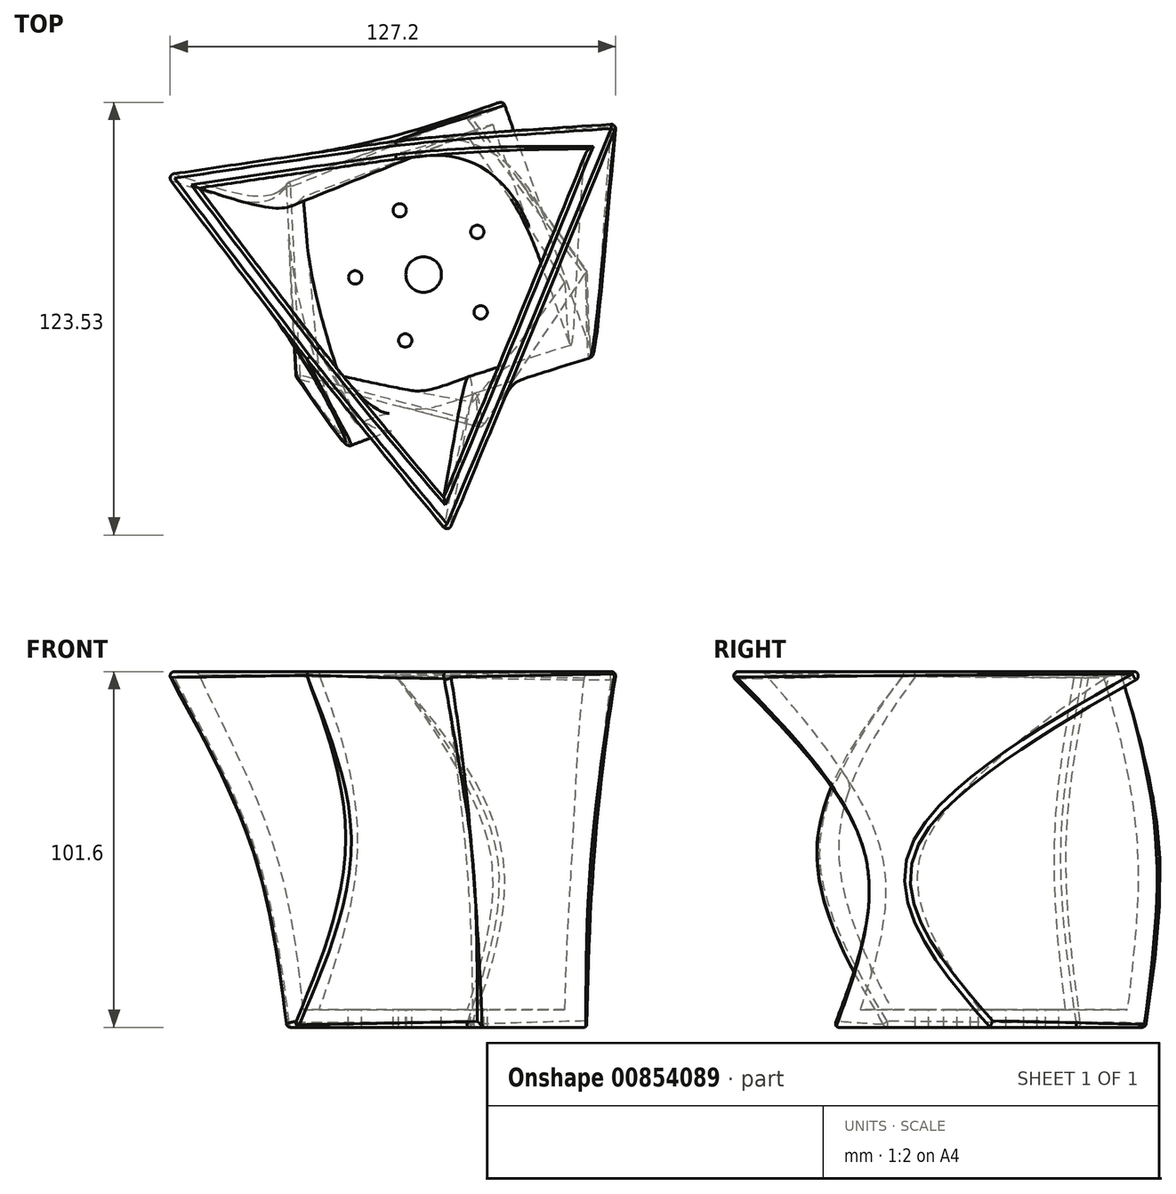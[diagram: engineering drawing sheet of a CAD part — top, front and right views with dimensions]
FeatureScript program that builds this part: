
annotation { "Feature Type Name" : "Feature", "Feature Type Description" : "" }
export const myFeature = defineFeature(function(context is Context, id is Id, definition is map)
    precondition{}
    {
        {
            var Q0;
            Q0=qCreatedBy(makeId("Top.planeOp"),FACE);
            var sketch = newSketch(context, id + "F0", { "sketchPlane" : qUnion([Q0])});
            skCircle(sketch, "E0.cCircle", {"center": v(0, 0) * mm, "radius": 38.1 * mm, "construction": true});
            skLineSegment(sketch, "E0.0", {"start": v(-39.1, 26.24) * mm, "end": v(12.87, 45.3) * mm});
            skLineSegment(sketch, "E0.1", {"start": v(12.87, 45.3) * mm, "end": v(47.06, 1.76) * mm});
            skLineSegment(sketch, "E0.2", {"start": v(47.06, 1.76) * mm, "end": v(16.21, -44.22) * mm});
            skLineSegment(sketch, "E0.3", {"start": v(16.21, -44.22) * mm, "end": v(-37.04, -29.08) * mm});
            skLineSegment(sketch, "E0.4", {"start": v(-37.04, -29.08) * mm, "end": v(-39.1, 26.24) * mm});
            skPoint(sketch, "E0.0.midPoint", {"position": v(-13.12, 35.77) * mm});
            skSolve(sketch);
        }
        {
            var Q0;
            Q0=qCreatedBy(makeId("Top.planeOp"),FACE);
            cPlane(context, id + "F1", {"entities" : qUnion([Q0]), "cplaneType" : CPlaneType.OFFSET, "offset" : 50.8 * mm, "width" : 152.4 * mm, "height" : 152.4 * mm});
        }
        {
            var Q0;
            Q0=qCreatedBy(id+"F1.planeOp",FACE);
            var sketch = newSketch(context, id + "F2", { "sketchPlane" : qUnion([Q0])});
            skCircle(sketch, "E1.cCircle", {"center": v(0, 0) * mm, "radius": 38.1 * mm, "construction": true});
            skLineSegment(sketch, "E1.0", {"start": v(-49.26, 21.84) * mm, "end": v(21.84, 49.26) * mm});
            skLineSegment(sketch, "E1.1", {"start": v(21.84, 49.26) * mm, "end": v(49.26, -21.84) * mm});
            skLineSegment(sketch, "E1.2", {"start": v(49.26, -21.84) * mm, "end": v(-21.84, -49.26) * mm});
            skLineSegment(sketch, "E1.3", {"start": v(-21.84, -49.26) * mm, "end": v(-49.26, 21.84) * mm});
            skPoint(sketch, "E1.0.midPoint", {"position": v(-13.71, 35.55) * mm});
            skSolve(sketch);
        }
        {
            var Q0;
            Q0=qCreatedBy(id+"F1.planeOp",FACE);
            cPlane(context, id + "F3", {"entities" : qUnion([Q0]), "cplaneType" : CPlaneType.OFFSET, "offset" : 50.8 * mm, "width" : 152.4 * mm, "height" : 152.4 * mm});
        }
        {
            var Q0;
            Q0=qCreatedBy(id+"F3.planeOp",FACE);
            var sketch = newSketch(context, id + "F4", { "sketchPlane" : qUnion([Q0])});
            skCircle(sketch, "E2.cCircle", {"center": v(-3.69, 0) * mm, "radius": 38.1 * mm, "construction": true});
            skLineSegment(sketch, "E2.0", {"start": v(-74.27, 28.73) * mm, "end": v(56.48, 46.76) * mm});
            skLineSegment(sketch, "E2.1", {"start": v(56.48, 46.76) * mm, "end": v(6.72, -75.49) * mm});
            skLineSegment(sketch, "E2.2", {"start": v(6.72, -75.49) * mm, "end": v(-74.27, 28.73) * mm});
            skPoint(sketch, "E2.0.midPoint", {"position": v(-8.9, 37.74) * mm});
            skSolve(sketch);
        }
        {
            var Q0;
            Q0=makeQuery(id+"F0.imprint","IMPRINT",FACE,{"disambiguationData":[TD([[makeQuery(id+"F0.imprint","IMPRINT",EDGE,{"derivedFrom":sQuery(id+"F0.wireOp",EDGE,"E0.0")}),-1.0]])]});
            var Q1;
            Q1=makeQuery(id+"F2.imprint","IMPRINT",FACE,{"disambiguationData":[TD([[makeQuery(id+"F2.imprint","IMPRINT",EDGE,{"derivedFrom":sQuery(id+"F2.wireOp",EDGE,"E1.0")}),-1.0]])]});
            var Q2;
            Q2=makeQuery(id+"F4.imprint","IMPRINT",FACE,{"disambiguationData":[TD([[makeQuery(id+"F4.imprint","IMPRINT",EDGE,{"derivedFrom":sQuery(id+"F4.wireOp",EDGE,"E2.0")}),-1.0]])]});
            loft(context, id + "F5", {"sheetProfilesArray" : [{ "sheetProfileEntities" : qUnion([Q0]) }, { "sheetProfileEntities" : qUnion([Q1]) }, { "sheetProfileEntities" : qUnion([Q2]) }]});
        }
        {
            var Q0;
            Q0=makeQuery(id+"F5.opLoft","CAP_FACE",FACE,{"disambiguationData":[OSD([makeQuery(id+"F4.imprint","IMPRINT",FACE,{"disambiguationData":[TD([[makeQuery(id+"F4.imprint","IMPRINT",EDGE,{"derivedFrom":sQuery(id+"F4.wireOp",EDGE,"E2.0")}),-1.0]])]})])],"isStart":true});
            shell(context, id + "F6", {"entities" : qUnion([Q0]), "thickness" : 5.08 * mm});
        }
        {
            var Q0;
            Q0=makeQuery(id+"F5.opLoft","CAP_FACE",FACE,{"disambiguationData":[OSD([makeQuery(id+"F4.imprint","IMPRINT",FACE,{"disambiguationData":[TD([[makeQuery(id+"F4.imprint","IMPRINT",EDGE,{"derivedFrom":sQuery(id+"F4.wireOp",EDGE,"E2.0")}),-1.0]])]})])],"isStart":true});
            var Q1;
            Q1=makeQuery(id+"F5.opLoft","SWEPT_FACE",FACE,{"disambiguationData":[OSD([sQuery(id+"F0.wireOp",EDGE,"E0.0"),sQuery(id+"F0.wireOp",EDGE,"E0.1"),sQuery(id+"F0.wireOp",EDGE,"E0.2"),sQuery(id+"F2.wireOp",EDGE,"E1.0"),sQuery(id+"F2.wireOp",EDGE,"E1.1"),sQuery(id+"F2.wireOp",EDGE,"E1.2"),sQuery(id+"F4.wireOp",EDGE,"E2.0"),sQuery(id+"F4.wireOp",EDGE,"E2.1"),sQuery(id+"F4.wireOp",EDGE,"E2.2")])]});
            var Q2;
            Q2=makeQuery(id+"F5.opLoft","SWEPT_FACE",FACE,{"disambiguationData":[OSD([sQuery(id+"F0.wireOp",EDGE,"E0.1"),sQuery(id+"F0.wireOp",EDGE,"E0.2"),sQuery(id+"F0.wireOp",EDGE,"E0.3"),sQuery(id+"F0.wireOp",EDGE,"E0.4"),sQuery(id+"F2.wireOp",EDGE,"E1.1"),sQuery(id+"F2.wireOp",EDGE,"E1.2"),sQuery(id+"F2.wireOp",EDGE,"E1.3"),sQuery(id+"F4.wireOp",EDGE,"E2.1"),sQuery(id+"F4.wireOp",EDGE,"E2.2")])]});
            var Q3;
            Q3=makeQuery(id+"F5.opLoft","SWEPT_FACE",FACE,{"disambiguationData":[OSD([sQuery(id+"F0.wireOp",EDGE,"E0.0"),sQuery(id+"F0.wireOp",EDGE,"E0.2"),sQuery(id+"F0.wireOp",EDGE,"E0.3"),sQuery(id+"F0.wireOp",EDGE,"E0.4"),sQuery(id+"F2.wireOp",EDGE,"E1.2"),sQuery(id+"F2.wireOp",EDGE,"E1.3"),sQuery(id+"F4.wireOp",EDGE,"E2.2")])]});
            var Q4;
            Q4=makeQuery(id+"F5.opLoft","SWEPT_FACE",FACE,{"disambiguationData":[OSD([sQuery(id+"F0.wireOp",EDGE,"E0.0"),sQuery(id+"F0.wireOp",EDGE,"E0.1"),sQuery(id+"F0.wireOp",EDGE,"E0.4"),sQuery(id+"F2.wireOp",EDGE,"E1.0"),sQuery(id+"F2.wireOp",EDGE,"E1.1"),sQuery(id+"F2.wireOp",EDGE,"E1.3"),sQuery(id+"F4.wireOp",EDGE,"E2.0"),sQuery(id+"F4.wireOp",EDGE,"E2.1"),sQuery(id+"F4.wireOp",EDGE,"E2.2")])]});
            var Q5;
            Q5=makeQuery(id+"F5.opLoft","MID_CAP_EDGE",EDGE,{"disambiguationData":[OSD([sQuery(id+"F0.wireOp",EDGE,"E0.0"),sQuery(id+"F0.wireOp",EDGE,"E0.3"),sQuery(id+"F0.wireOp",EDGE,"E0.4")])],"capPos":0.0});
            fillet(context, id + "F7", {"entities" : qUnion([Q0, Q1, Q2, Q3, Q4, Q5]), "radius" : 1.27 * mm, "tangentPropagation" : true, "allowEdgeOverflow" : false});
        }
        {
            var Q0;
            Q0=makeQuery(id+"F6.opShell","OFFSET_FACE",FACE,{"disambiguationData":[OSD([makeQuery(id+"F0.imprint","IMPRINT",FACE,{"disambiguationData":[TD([[makeQuery(id+"F0.imprint","IMPRINT",EDGE,{"derivedFrom":sQuery(id+"F0.wireOp",EDGE,"E0.0")}),-1.0]])]})])]});
            var sketch = newSketch(context, id + "F8", { "sketchPlane" : qUnion([Q0])});
            skCircle(sketch, "E3", {"center": v(-6.83, 18.33) * mm, "radius": 1.9 * mm});
            skCircle(sketch, "E4.1.0", {"center": v(-19.54, -0.83) * mm, "radius": 1.9 * mm});
            skCircle(sketch, "E4.2.0", {"center": v(-5.25, -18.84) * mm, "radius": 1.9 * mm});
            skCircle(sketch, "E4.3.0", {"center": v(16.3, -10.81) * mm, "radius": 1.9 * mm});
            skCircle(sketch, "E4.4.0", {"center": v(15.32, 12.16) * mm, "radius": 1.9 * mm});
            skPoint(sketch, "E4.center", {"position": v(0, 0) * mm});
            skSolve(sketch);
        }
        {
            var Q0;
            Q0=qSketchRegion(id+"F8",true);
            extrude(context, id + "F9", {"entities" : qUnion([Q0]), "operationType" : NewBodyOperationType.REMOVE, "endBound" : BoundingType.THROUGH_ALL, "oppositeDirection" : true, "depth" : 25.4 * mm, "offsetDistance" : 25.4 * mm});
        }
        {
            var Q0;
            Q0=makeQuery(id+"F6.opShell","OFFSET_FACE",FACE,{"disambiguationData":[OSD([makeQuery(id+"F0.imprint","IMPRINT",FACE,{"disambiguationData":[TD([[makeQuery(id+"F0.imprint","IMPRINT",EDGE,{"derivedFrom":sQuery(id+"F0.wireOp",EDGE,"E0.0")}),-1.0]])]})])]});
            var sketch = newSketch(context, id + "F10", { "sketchPlane" : qUnion([Q0])});
            skCircle(sketch, "E5", {"center": v(0, 0) * mm, "radius": 5.08 * mm});
            skSolve(sketch);
        }
        {
            var Q0;
            Q0=qSketchRegion(id+"F10",true);
            extrude(context, id + "F11", {"entities" : qUnion([Q0]), "operationType" : NewBodyOperationType.REMOVE, "endBound" : BoundingType.THROUGH_ALL, "oppositeDirection" : true, "depth" : 25.4 * mm, "offsetDistance" : 25.4 * mm});
        }
    });
